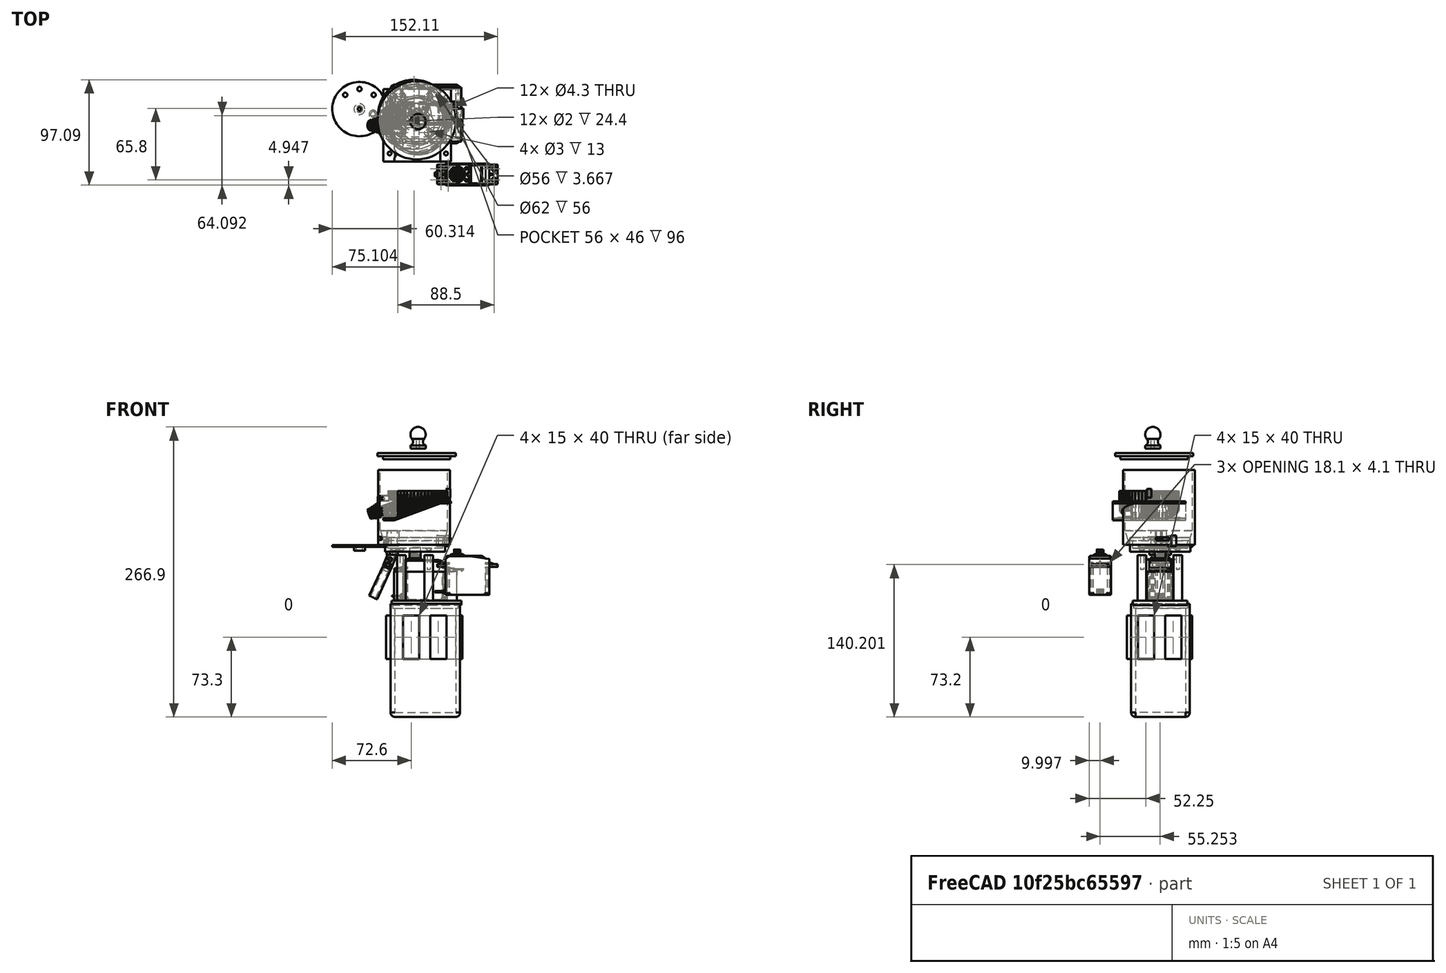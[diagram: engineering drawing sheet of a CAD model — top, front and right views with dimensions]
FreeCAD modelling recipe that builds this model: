
FCSTD DOCUMENT  (FreeCAD 0.21R33771 (Git))
Label: all_parts_chute_with_mount_v3
License: All rights reserved
LicenseURL: http://en.wikipedia.org/wiki/All_rights_reserved
objects: Part::Cylinder×37, Part::Cut×30, Part::MultiFuse×25, Part::Box×19, Part::Feature×18, Part::FeaturePython×10, Sketcher::SketchObject×3, Part::Cone×2, Part::Extrusion×2, Mesh::Feature×1, Part::Fillet×1, Part::Chamfer×1, Part::Thickness×1, PartDesign::Revolution×1, PartDesign::Body×1, Part::Wedge×1
note: 149 computed .brp shape members not serialized (recipe doc carries the construction recipe); baked Part::Feature solids carry a one-line shape summary decoded from their .brp

FEATURE [Part::Box] Box014  label="Cube014"
  AttacherType = Attacher::AttachEngine3D
  Height = 2
  Length = 7
  Placement = pos=(66.2,37.3,74.6) rot=(0,0,1;0rad)
  Width = 4.2
FEATURE [Part::Cylinder] Cylinder022
  Angle = 360
  AttacherType = Attacher::AttachEngine3D
  FirstAngle = 0
  Height = 20
  Placement = pos=(15.5,39.3,51.5) rot=(0,1,0;0.366519rad)
  Radius = 3
  SecondAngle = 0
FEATURE [Part::Box] Box015  label="Cube015"
  AttacherType = Attacher::AttachEngine3D
  Height = 10
  Length = 10
  Placement = pos=(7,34.3,72) rot=(0,0,1;0rad)
  Width = 13
FEATURE [Mesh::Feature] Base_V7  label="Base V7"
FEATURE [Part::Feature] Base_V7001_solid  label="hopper (Solid)"
  shape: bbox 76.98 x 66.8 x 28.84 mm, 5900 faces (baked)
FEATURE [Part::Feature] Shape001
  Placement = pos=(47,50.7,-44.8) rot=(0,0,1;3.14159rad)
  shape: bbox 57.75 x 20 x 41.74 mm, 378 faces, 4 solids (baked)
FEATURE [Part::Cylinder] cylinder010  label="servo_central_shaft"
  Angle = 360
  AttacherType = Attacher::AttachEngine3D
  FirstAngle = 0
  Height = 10
  Placement = pos=(37.55,50.7,-7) rot=(0,0,1;0rad)
  Radius = 5
  SecondAngle = 0
FEATURE [Part::Box] Box  label="Cube"
  AttacherType = Attacher::AttachEngine3D
  Height = 27.5
  Length = 58
  Placement = pos=(18,38.6,-47) rot=(0,0,1;0rad)
  Width = 24
FEATURE [Part::Box] Box016  label="Cube016"
  AttacherType = Attacher::AttachEngine3D
  Height = 29.5
  Length = 53
  Placement = pos=(13,46,-44) rot=(0,0,1;0rad)
  Width = 9
FEATURE [Part::Cut] Cut
  Base = -> Box
  Tool = -> Box016
FEATURE [Part::Box] Box017  label="Cube017"
  AttacherType = Attacher::AttachEngine3D
  Height = 29.5
  Length = 10
  Placement = pos=(17,46.6,-46) rot=(0,0,1;0rad)
  Width = 8
FEATURE [Part::Cut] Cut019
  Base = -> Cut
  Tool = -> Box017
FEATURE [Part::Box] Box018  label="Cube018"
  AttacherType = Attacher::AttachEngine3D
  Height = 27.5
  Length = 41
  Placement = pos=(0.5,50.4,-44.2) rot=(0,0,1;0rad)
  Width = 20.4
FEATURE [Part::Fillet] Fillet
  Base = -> Box018
  Edges = 4 edges r=1: [Edge1,Edge3,Edge5,Edge7]
  Placement = pos=(25.85,-9.87885,-1.16822) rot=(0,0,1;0rad)
FEATURE [Part::Cut] Cut020
  Base = -> Cut019
  Tool = -> Fillet
FEATURE [Part::Box] Box020  label="base_plate"
  AttacherType = Attacher::AttachEngine3D
  Height = 4
  Length = 64
  Placement = pos=(16,25.6,-50) rot=(0,0,1;0rad)
  Width = 50
FEATURE [Part::Feature] BOLTS_part  label="Hex socket countersunk head screw M3 20.0"
  Placement = pos=(25,67,2.1) rot=(0,1,0;3.14159rad)
  shape: bbox 6 x 6 x 20 mm, 12 faces (baked)
FEATURE [Part::Feature] BOLTS_part001  label="Hex socket countersunk head screw M3 20.001"
  Placement = pos=(50,67,2.1) rot=(0,1,0;3.14159rad)
  shape: bbox 6 x 6 x 20 mm, 12 faces (baked)
FEATURE [Part::Feature] BOLTS_part002  label="Hex socket countersunk head screw M3 20.002"
  Placement = pos=(50,34,2.1) rot=(0,1,0;3.14159rad)
  shape: bbox 6 x 6 x 20 mm, 12 faces (baked)
FEATURE [Part::Feature] BOLTS_part003  label="Hex socket countersunk head screw M3 20.003"
  Placement = pos=(25,34,2.1) rot=(0,1,0;3.14159rad)
  shape: bbox 6 x 6 x 20 mm, 12 faces (baked)
FEATURE [Part::Cylinder] Cylinder024
  Angle = 360
  AttacherType = Attacher::AttachEngine3D
  FirstAngle = 0
  Height = 45
  Placement = pos=(50,67,-49) rot=(0,0,1;0rad)
  Radius = 4
  SecondAngle = 0
FEATURE [Part::Cylinder] Cylinder025
  Angle = 360
  AttacherType = Attacher::AttachEngine3D
  FirstAngle = 0
  Height = 45
  Placement = pos=(25,34,-49) rot=(0,0,1;0rad)
  Radius = 4
  SecondAngle = 0
FEATURE [Part::Cylinder] Cylinder026
  Angle = 360
  AttacherType = Attacher::AttachEngine3D
  FirstAngle = 0
  Height = 45
  Placement = pos=(25,67,-49) rot=(0,0,1;0rad)
  Radius = 4
  SecondAngle = 0
FEATURE [Part::Cylinder] Cylinder027
  Angle = 360
  AttacherType = Attacher::AttachEngine3D
  FirstAngle = 0
  Height = 45
  Placement = pos=(50,34,-49) rot=(0,0,1;0rad)
  Radius = 4
  SecondAngle = 0
FEATURE [Part::Feature] Shape002  label="led2"
  Placement = pos=(14.5,42.3,-8) rot=(-1,0,0;1.5708rad)
  shape: bbox 3.686 x 11.4 x 3.686 mm, 26 faces, 3 solids (baked)
FEATURE [Part::Feature] Shape003  label="led1"
  Placement = pos=(14.5,59.1,-8) rot=(1,0,0;1.5708rad)
  shape: bbox 3.686 x 11.4 x 3.686 mm, 26 faces, 3 solids (baked)
FEATURE [Part::Feature] BOLTS_part004  label="Hex socket countersunk head screw M3 20.004"
  Placement = pos=(25,34,3) rot=(0,1,0;3.14159rad)
  shape: bbox 6 x 6 x 20 mm, 12 faces (baked)
FEATURE [Part::Feature] BOLTS_part005  label="Hex socket countersunk head screw M3 20.005"
  Placement = pos=(50,34,3) rot=(0,1,0;3.14159rad)
  shape: bbox 6 x 6 x 20 mm, 12 faces (baked)
FEATURE [Part::Feature] BOLTS_part006  label="Hex socket countersunk head screw M3 20.006"
  Placement = pos=(50,67,3) rot=(0,1,0;3.14159rad)
  shape: bbox 6 x 6 x 20 mm, 12 faces (baked)
FEATURE [Part::Feature] BOLTS_part007  label="Hex socket countersunk head screw M3 20.007"
  Placement = pos=(25,67,3) rot=(0,1,0;3.14159rad)
  shape: bbox 6 x 6 x 20 mm, 12 faces (baked)
FEATURE [Part::Cylinder] Cylinder032
  Angle = 360
  AttacherType = Attacher::AttachEngine3D
  FirstAngle = 0
  Height = 48
  Placement = pos=(50,67,-43) rot=(0,0,1;0rad)
  Radius = 1.4
  SecondAngle = 0
FEATURE [Part::Cylinder] Cylinder033
  Angle = 360
  AttacherType = Attacher::AttachEngine3D
  FirstAngle = 0
  Height = 48
  Placement = pos=(25,34,-43) rot=(0,0,1;0rad)
  Radius = 1.4
  SecondAngle = 0
FEATURE [Part::Cylinder] Cylinder034
  Angle = 360
  AttacherType = Attacher::AttachEngine3D
  FirstAngle = 0
  Height = 48
  Placement = pos=(25,67,-42) rot=(0,0,1;0rad)
  Radius = 1.4
  SecondAngle = 0
FEATURE [Part::Cylinder] Cylinder035
  Angle = 360
  AttacherType = Attacher::AttachEngine3D
  FirstAngle = 0
  Height = 48
  Placement = pos=(50,34,-43) rot=(0,0,1;0rad)
  Radius = 1.4
  SecondAngle = 0
FEATURE [Part::Cut] Cut030
  Base = -> Cylinder024
  Tool = -> BOLTS_part006
FEATURE [Part::Cut] Cut031
  Base = -> Cylinder025
  Tool = -> BOLTS_part004
FEATURE [Part::Cut] Cut032
  Base = -> Cylinder026
  Tool = -> BOLTS_part007
FEATURE [Part::Cut] Cut033
  Base = -> Cylinder027
  Tool = -> BOLTS_part005
FEATURE [Part::MultiFuse] Fusion011  label="fusion"
  Shapes = -> [Cut020,Cut030,Cut031,Cut032,Cut033,Box020]
FEATURE [Part::Cylinder] Cylinder039
  Angle = 360
  AttacherType = Attacher::AttachEngine3D
  FirstAngle = 0
  Height = 21
  Placement = pos=(0,10,6) rot=(1,0,0;1.5708rad)
  Radius = 1.6
  SecondAngle = 0
FEATURE [Part::FeaturePython] Tube003  # WARN: FeaturePython — macro-defined, semantics opaque (R4)
  AttacherType = Attacher::AttachEngine3D
  Height = 5
  InnerRadius = 1.5
  OuterRadius = 2.5
  Placement = pos=(0,2.05,6) rot=(-1,0,0;1.5708rad)
FEATURE [Part::FeaturePython] Tube004  # WARN: FeaturePython — macro-defined, semantics opaque (R4)
  AttacherType = Attacher::AttachEngine3D
  Height = 5
  InnerRadius = 1.5
  OuterRadius = 2.5
  Placement = pos=(0,-2.05,6) rot=(1,0,0;1.5708rad)
FEATURE [Part::Box] Box021  label="Cube019"
  AttacherType = Attacher::AttachEngine3D
  Height = 10
  Length = 20
  Placement = pos=(1.17,-11.94,17.9) rot=(0,0,1;0rad)
  Width = 24
FEATURE [Part::FeaturePython] Tube001  # WARN: FeaturePython — macro-defined, semantics opaque (R4)
  AttacherType = Attacher::AttachEngine3D
  Height = 3
  InnerRadius = 15
  OuterRadius = 27.7
  Placement = pos=(40.45,39.4,63.6) rot=(0,0,1;0rad)
FEATURE [Part::FeaturePython] Tube002  # WARN: FeaturePython — macro-defined, semantics opaque (R4)
  AttacherType = Attacher::AttachEngine3D
  Height = 13
  InnerRadius = 25.3
  OuterRadius = 27.7
  Placement = pos=(40.45,39.4,63.6) rot=(0,0,1;0rad)
FEATURE [Part::MultiFuse] Fusion009
  Shapes = -> [Box014,Tube001,Tube002]
FEATURE [Part::Cut] Cut014  label="cut"
  Base = -> Fusion009
  Tool = -> Cylinder022
FEATURE [Part::Cut] Cut036
  Base = -> Cut014
  Placement = pos=(-2.9,11.3,-64.5) rot=(0,0,1;0rad)
  Tool = -> Box015
FEATURE [Part::MultiFuse] Fusion
  Shapes = -> [BOLTS_part003,Cylinder033]
FEATURE [Part::MultiFuse] Fusion013
  Shapes = -> [BOLTS_part002,Cylinder035]
FEATURE [Part::MultiFuse] Fusion014
  Shapes = -> [BOLTS_part001,Cylinder032]
FEATURE [Part::MultiFuse] Fusion015
  Shapes = -> [BOLTS_part,Cylinder034]
FEATURE [Part::Cut] Cut037
  Base = -> Cut036
  Tool = -> Fusion
FEATURE [Part::Cut] Cut038
  Base = -> Cut037
  Tool = -> Fusion013
FEATURE [Part::Cut] Cut039
  Base = -> Cut038
  Tool = -> Fusion015
FEATURE [Part::Cut] Cut040
  Base = -> Cut039
  Tool = -> Fusion014
FEATURE [Part::Feature] BOLTS_part009  label="Hex socket countersunk head screw M3 20.008"
  Placement = pos=(50,34,2.1) rot=(0,1,0;3.14159rad)
  shape: bbox 6 x 6 x 20 mm, 12 faces (baked)
FEATURE [Part::Cylinder] Cylinder040
  Angle = 360
  AttacherType = Attacher::AttachEngine3D
  FirstAngle = 0
  Height = 48
  Placement = pos=(50,34,-43) rot=(0,0,1;0rad)
  Radius = 1.4
  SecondAngle = 0
FEATURE [Part::MultiFuse] Fusion016
  Placement = pos=(-32,9,0) rot=(0,0,1;0rad)
  Shapes = -> [BOLTS_part009,Cylinder040]
FEATURE [Part::Feature] BOLTS_part010  label="Hex socket countersunk head screw M3 20.009"
  Placement = pos=(50,34,2.1) rot=(0,1,0;3.14159rad)
  shape: bbox 6 x 6 x 20 mm, 12 faces (baked)
FEATURE [Part::Cylinder] Cylinder041
  Angle = 360
  AttacherType = Attacher::AttachEngine3D
  FirstAngle = 0
  Height = 48
  Placement = pos=(50,34,-43) rot=(0,0,1;0rad)
  Radius = 1.4
  SecondAngle = 0
FEATURE [Part::MultiFuse] Fusion017
  Placement = pos=(-32,24,0) rot=(0,0,1;0rad)
  Shapes = -> [BOLTS_part010,Cylinder041]
FEATURE [Part::Box] Box022  label="Cube020"
  AttacherType = Attacher::AttachEngine3D
  Height = 3
  Length = 10
  Placement = pos=(3,-10,15) rot=(0,0,1;0rad)
  Width = 20
FEATURE [Part::Cylinder] Cylinder
  Angle = 360
  AttacherType = Attacher::AttachEngine3D
  FirstAngle = 0
  Height = 18
  Radius = 4
  SecondAngle = 0
FEATURE [Part::Cut] Cut043
  Base = -> Cylinder
  Tool = -> Cylinder039
FEATURE [Part::MultiFuse] Fusion018
  Placement = pos=(2,0,0) rot=(0,1,0;0.366519rad)
  Shapes = -> [Tube003,Tube004,Cut043]
FEATURE [Part::MultiFuse] Fusion019
  Shapes = -> [Fusion018,Box022]
FEATURE [Part::Feature] BOLTS_part011  label="Hex socket countersunk head screw M3 20.010"
  Placement = pos=(50,34,2.1) rot=(0,1,0;3.14159rad)
  shape: bbox 6 x 6 x 20 mm, 12 faces (baked)
FEATURE [Part::Cylinder] Cylinder044
  Angle = 360
  AttacherType = Attacher::AttachEngine3D
  FirstAngle = 0
  Height = 48
  Placement = pos=(50,34,-43) rot=(0,0,1;0rad)
  Radius = 1.4
  SecondAngle = 0
FEATURE [Part::MultiFuse] Fusion021
  Placement = pos=(-32,9,0) rot=(0,0,1;0rad)
  Shapes = -> [BOLTS_part011,Cylinder044]
FEATURE [Part::Feature] BOLTS_part012  label="Hex socket countersunk head screw M3 20.011"
  Placement = pos=(50,34,2.1) rot=(0,1,0;3.14159rad)
  shape: bbox 6 x 6 x 20 mm, 12 faces (baked)
FEATURE [Part::Cylinder] Cylinder045
  Angle = 360
  AttacherType = Attacher::AttachEngine3D
  FirstAngle = 0
  Height = 48
  Placement = pos=(50,34,-43) rot=(0,0,1;0rad)
  Radius = 1.4
  SecondAngle = 0
FEATURE [Part::MultiFuse] Fusion022
  Placement = pos=(-32,24,0) rot=(0,0,1;0rad)
  Shapes = -> [BOLTS_part012,Cylinder045]
FEATURE [Part::Cut] Cut047
  Base = -> Cut040
  Tool = -> Fusion016
FEATURE [Part::Cut] Cut048
  Base = -> Cut047
  Tool = -> Fusion017
FEATURE [Part::Feature] Shape004  label="Servo_motor"
  Placement = pos=(46.0641,51.1469,-44.6487) rot=(0,0,1;3.14159rad)
  shape: bbox 57.75 x 20 x 41.74 mm, 378 faces, 4 solids (baked)
FEATURE [Part::Box] Box012  label="Cube012"
  AttacherType = Attacher::AttachEngine3D
  Height = 10
  Length = 10
  Placement = pos=(7,36.17,76) rot=(0,0,1;0rad)
  Width = 6
FEATURE [Part::Box] Box013  label="Cube013"
  AttacherType = Attacher::AttachEngine3D
  Height = 3
  Length = 14
  Placement = pos=(64,38,58) rot=(0,0,1;0rad)
  Width = 12
FEATURE [Part::Cone] Cone
  Angle = 360
  AttacherType = Attacher::AttachEngine3D
  Height = 14
  Placement = pos=(40,40.65,53) rot=(0,0,1;0rad)
  Radius1 = 26.5
  Radius2 = 31
FEATURE [Part::Cylinder] Cylinder019
  Angle = 360
  AttacherType = Attacher::AttachEngine3D
  FirstAngle = 0
  Height = 13
  Placement = pos=(40,40.65,54) rot=(0,0,1;0rad)
  Radius = 33
  SecondAngle = 0
FEATURE [Part::Cylinder] Cylinder020
  Angle = 360
  AttacherType = Attacher::AttachEngine3D
  FirstAngle = 0
  Height = 13
  Placement = pos=(40,39.2,54) rot=(0,0,1;0rad)
  Radius = 25
  SecondAngle = 0
FEATURE [Part::Cylinder] Cylinder021
  Angle = 360
  AttacherType = Attacher::AttachEngine3D
  FirstAngle = 0
  Height = 4
  Placement = pos=(40,40.65,54) rot=(0,0,1;0rad)
  Radius = 28
  SecondAngle = 0
FEATURE [Sketcher::SketchObject] Sketch001
  FullyConstrained = true
  MapMode = 2
  Placement = pos=(0,5,65) rot=(0,0,1;0rad)
  sketch-geometry (8):
    g0: ArcOfCircle CenterX=20.555 CenterY=41.4363 CenterZ=0 NormalX=0 NormalY=0 NormalZ=1 AngleXU=0 Radius=4.5 StartAngle=3.17145 EndAngle=4.38602
    g1: ArcOfCircle CenterX=24.0176 CenterY=34.022 CenterZ=0 NormalX=0 NormalY=0 NormalZ=1 AngleXU=0 Radius=2 StartAngle=5.10518 EndAngle=7.46119
    g2: ArcOfCircle CenterX=20.5312 CenterY=26.882 CenterZ=0 NormalX=0 NormalY=0 NormalZ=1 AngleXU=0 Radius=4.5 StartAngle=1.8916 EndAngle=3.11914
    g3: LineSegment StartX=19.1123 StartY=31.1525 StartZ=0 EndX=24.7831 EndY=32.1743 EndZ=0
    g4: LineSegment StartX=19.1123 StartY=37.1738 StartZ=0 EndX=24.7831 EndY=35.8697 EndZ=0
    g5: LineSegment StartX=16.057 StartY=41.302 StartZ=0 EndX=15.8089 EndY=41.3763 EndZ=0
    g6: LineSegment StartX=15.8133 StartY=26.9187 StartZ=0 EndX=16.0324 EndY=26.9831 EndZ=0
    g7: ArcOfCircle CenterX=39.7432 CenterY=34.1548 CenterZ=0 NormalX=0 NormalY=0 NormalZ=1 AngleXU=0 Radius=25 StartAngle=2.84856 EndAngle=3.43524
  constraints (28):
    c: Coincident(g3,g2)
    c: Coincident(g3,g1)
    c: Coincident(g4,g0)
    c: Coincident(g4,g1)
    c: Coincident(g5,g0)
    c: Coincident(g6,g2)
    c: Coincident(g7,g6)
    c: Coincident(g7,g5)
    c: Radius(g2) = 4.5
    c: Radius(g0) = 4.5
    c: Radius(g1) = 2
    c: Radius(g7) = 25
    c: DistanceX(g5) = 15.8089
    c: DistanceY(g5) = 41.3763
    c: DistanceX(g2) = 16.0324
    c: DistanceY(g2) = 26.9831
    c: DistanceX(g3) = 19.1123
    c: DistanceY(g3) = 31.1525
    c: DistanceX(g2,g0) = 0
    c: DistanceX(g3,g1) = 0
    c: DistanceX(g1) = 24.7831
    c: DistanceY(g1) = 32.1743
    c: DistanceX(g5) = 16.057
    c: DistanceY(g5) = 41.302
    c: DistanceX(g7) = 15.8133
    c: DistanceY(g7) = 26.9187
    c: DistanceY(g1) = 35.8697
    c: DistanceY(g0) = 37.1738
FEATURE [Part::Extrusion] Extrude001
  Base = -> Sketch001
  Dir = (0,0,1)
  DirMode = 2
  FaceMakerClass = Part::FaceMakerBullseye
  LengthFwd = 14
  LengthRev = 0
  Placement = pos=(0,0,7) rot=(0,0,1;0rad)
  Solid = true
  Symmetric = false
FEATURE [Part::MultiFuse] Fusion006  label="pellet_sorter"
  Placement = pos=(0,1.5,-19) rot=(0,0,1;0rad)
  Shapes = -> [Box012,Extrude001]
FEATURE [Part::FeaturePython] Tube  # WARN: FeaturePython — macro-defined, semantics opaque (R4)
  AttacherType = Attacher::AttachEngine3D
  Height = 69
  InnerRadius = 31
  OuterRadius = 33
  Placement = pos=(40,40.65,54) rot=(0,0,1;0rad)
FEATURE [Part::MultiFuse] Fusion010
  Shapes = -> [Tube,Cylinder019,Cylinder020]
FEATURE [Part::Cut] Cut015
  Base = -> Fusion010
  Tool = -> Cone
FEATURE [Part::Cut] Cut016
  Base = -> Cut015
  Tool = -> Cylinder021
FEATURE [Part::MultiFuse] Fusion024
  Shapes = -> [Fusion006,Cut016]
FEATURE [Part::Cut] Cut017  label="cut002"
  Base = -> Fusion024
  Placement = pos=(2.75889,1.57596,-47) rot=(0,0,1;0.15708rad)
  Tool = -> Box013
FEATURE [Part::Cylinder] Cylinder047
  Angle = 360
  AttacherType = Attacher::AttachEngine3D
  FirstAngle = 0
  Height = 3
  Radius = 36
  SecondAngle = 0
FEATURE [Part::Cylinder] Cylinder048
  Angle = 360
  AttacherType = Attacher::AttachEngine3D
  FirstAngle = 0
  Height = 6
  Radius = 31
  SecondAngle = 0
FEATURE [Part::MultiFuse] Fusion025  label="cut001"
  Placement = pos=(39,45.2,90) rot=(1,0,0;3.14159rad)
  Shapes = -> [Cylinder047,Cylinder048]
FEATURE [Part::Cylinder] cylinder012
  Angle = 360
  AttacherType = Attacher::AttachEngine3D
  FirstAngle = 0
  Height = 1.5
  Radius = 25
  SecondAngle = 0
FEATURE [Part::Cylinder] cylinder013
  Angle = 360
  AttacherType = Attacher::AttachEngine3D
  FirstAngle = 0
  Height = 1
  Placement = pos=(18.5,0,0) rot=(0,0,1;0rad)
  Radius = 2
  SecondAngle = 0
FEATURE [Part::Cylinder] cylinder014
  Angle = 360
  AttacherType = Attacher::AttachEngine3D
  FirstAngle = 0
  Height = 1
  Placement = pos=(13.0815,13.0815,0) rot=(0,0,1;0.785398rad)
  Radius = 2
  SecondAngle = 0
FEATURE [Part::Cylinder] cylinder015
  Angle = 360
  AttacherType = Attacher::AttachEngine3D
  FirstAngle = 0
  Height = 1
  Placement = pos=(0,18.5,0) rot=(0,0,1;1.5708rad)
  Radius = 2
  SecondAngle = 0
FEATURE [Part::Cylinder] cylinder016
  Angle = 360
  AttacherType = Attacher::AttachEngine3D
  FirstAngle = 0
  Height = 1
  Placement = pos=(-13.0815,13.0815,0) rot=(0,0,1;2.35619rad)
  Radius = 2
  SecondAngle = 0
FEATURE [Part::Cylinder] cylinder017
  Angle = 360
  AttacherType = Attacher::AttachEngine3D
  FirstAngle = 0
  Height = 1
  Placement = pos=(-18.5,2e-15,0) rot=(0,0,1;3.14159rad)
  Radius = 2
  SecondAngle = 0
FEATURE [Part::Cylinder] cylinder018
  Angle = 360
  AttacherType = Attacher::AttachEngine3D
  FirstAngle = 0
  Height = 5
  Placement = pos=(-13.0815,-13.0815,0) rot=(0,0,1;3.92699rad)
  Radius = 2
  SecondAngle = 0
FEATURE [Part::Cylinder] cylinder019
  Angle = 360
  AttacherType = Attacher::AttachEngine3D
  FirstAngle = 0
  Height = 5
  Placement = pos=(0,-18.5,0) rot=(0,0,-1;1.5708rad)
  Radius = 2
  SecondAngle = 0
FEATURE [Part::Cylinder] cylinder020
  Angle = 360
  AttacherType = Attacher::AttachEngine3D
  FirstAngle = 0
  Height = 5
  Placement = pos=(13.0815,-13.0815,0) rot=(0,0,-1;0.785398rad)
  Radius = 2
  SecondAngle = 0
FEATURE [Part::MultiFuse] Group001
  Placement = pos=(0,0,-1) rot=(0,0,1;0rad)
  Shapes = -> [cylinder013,cylinder014,cylinder015,cylinder016,cylinder017,cylinder018,cylinder019,cylinder020]
FEATURE [Part::Feature] Shape005
  Placement = pos=(85.6641,-4.55315,-40.6487) rot=(0,0,1;3.14159rad)
  shape: bbox 57.75 x 20 x 41.74 mm, 378 faces, 4 solids (baked)
FEATURE [Part::Cylinder] cylinder021  label="servo_central_shaft002"
  Angle = 360
  AttacherType = Attacher::AttachEngine3D
  FirstAngle = 0
  Height = 5
  Radius = 5
  SecondAngle = 0
FEATURE [Sketcher::SketchObject] Sketch002
  FullyConstrained = false
  MapMode = 5
  Placement = pos=(85.6641,-4.55315,1.09128) rot=(0,0,1;3.14159rad)
  Support = -> [Shape005]
  sketch-geometry (1):
    g0: Circle CenterX=9.4502 CenterY=-0.000218 CenterZ=0 NormalX=0 NormalY=0 NormalZ=1 AngleXU=0 Radius=3
  constraints (1):
    c: Radius(g0) = 3
FEATURE [Part::Extrusion] Extrude002
  Base = -> Sketch002
  Dir = (0,0,1)
  DirMode = 2
  FaceMakerClass = Part::FaceMakerBullseye
  LengthFwd = 4
  LengthRev = 3.4
  Placement = pos=(-76.21,4.55,3) rot=(0,0,1;0rad)
  Solid = true
  Symmetric = false
FEATURE [Part::Cylinder] Cylinder049
  Angle = 360
  AttacherType = Attacher::AttachEngine3D
  FirstAngle = 0
  Height = 19
  Placement = pos=(0,0,-1) rot=(0,0,1;0rad)
  Radius = 1.5
  SecondAngle = 0
FEATURE [Part::MultiFuse] Fusion026
  Shapes = -> [Group001,Extrude002,Cylinder049]
FEATURE [Part::MultiFuse] Fusion027
  Shapes = -> [cylinder012,cylinder021]
FEATURE [Part::Cut] Cut050  label="Rotor"
  Base = -> Fusion027
  Placement = pos=(-13.7,55.5,5) rot=(1,0,0;3.14159rad)
  Tool = -> Fusion026
FEATURE [Part::Cone] Cone001
  Angle = 360
  AttacherType = Attacher::AttachEngine3D
  Height = 11
  Placement = pos=(0,-29,0) rot=(0,0,1;0rad)
  Radius1 = 2
  Radius2 = 3
FEATURE [Part::Cylinder] Cylinder050
  Angle = 360
  AttacherType = Attacher::AttachEngine3D
  FirstAngle = 0
  Height = 10
  Placement = pos=(0,-29,-10) rot=(0,0,1;0rad)
  Radius = 2
  SecondAngle = 0
FEATURE [Part::Cylinder] Cylinder051
  Angle = 360
  AttacherType = Attacher::AttachEngine3D
  FirstAngle = 0
  Height = 14
  Placement = pos=(0,-29,11) rot=(0,0,1;0rad)
  Radius = 2
  SecondAngle = 0
FEATURE [Part::MultiFuse] Fusion028
  Placement = pos=(5,29,8) rot=(0,1,0;0.366519rad)
  Shapes = -> [Cone001,Cylinder050,Cylinder051]
FEATURE [Part::MultiFuse] Fusion020
  Shapes = -> [Box021,Fusion028]
FEATURE [Part::Cut] Cut044  label="foodchute"
  Base = -> Fusion019
  Placement = pos=(8.45427,50.6,-18.8) rot=(0,0,1;0rad)
  Tool = -> Fusion020
FEATURE [Part::Chamfer] Chamfer
  Base = -> Cut044
  Edges = 2 edges r=3: [Edge1,Edge3]
FEATURE [Part::Cut] Cut045
  Base = -> Chamfer
  Tool = -> Fusion021
FEATURE [Part::Cut] Cut046
  Base = -> Cut045
  Tool = -> Fusion022
FEATURE [Part::FeaturePython] Tube005  # WARN: FeaturePython — macro-defined, semantics opaque (R4)
  AttacherType = Attacher::AttachEngine3D
  Height = 4
  InnerRadius = 3
  OuterRadius = 5
  Placement = pos=(10.2596,50.6,-19.2425) rot=(0,1,0;0.401426rad)
FEATURE [Part::Cut] Cut051  label="chute_with_mount"
  Base = -> Cut046
  Tool = -> Tube005
FEATURE [Part::Box] Box023  label="Cube021"
  AttacherType = Attacher::AttachEngine3D
  Height = 100
  Length = 56
  Width = 46
FEATURE [Part::Thickness] Thickness
  Faces = -> Box023 [Face5]
  Intersection = false
  Join = 0
  Mode = 0
  SelfIntersection = false
  Value = 4
FEATURE [Part::Box] Box001  label="Cube001"
  AttacherType = Attacher::AttachEngine3D
  Height = 4
  Length = 60
  Placement = pos=(-2,-2,0) rot=(0,0,1;0rad)
  Width = 50
FEATURE [Part::Box] Box024  label="Cube022"
  AttacherType = Attacher::AttachEngine3D
  Height = 40
  Length = 15
  Placement = pos=(26.4,20,-99.7) rot=(0,0,1;0rad)
  Width = 60
FEATURE [Part::Box] Box025  label="Cube023"
  AttacherType = Attacher::AttachEngine3D
  Height = 40
  Length = 70
  Placement = pos=(10.9,30.2,-99.8) rot=(0,0,1;0rad)
  Width = 15
FEATURE [Part::Cylinder] Cylinder052
  Angle = 360
  AttacherType = Attacher::AttachEngine3D
  FirstAngle = 0
  Height = 10
  Placement = pos=(39,45.2,83) rot=(0,0,1;0rad)
  Radius = 1.5
  SecondAngle = 0
FEATURE [Part::Cut] Cut055  label="Cap"
  Base = -> Fusion025
  Tool = -> Cylinder052
FEATURE [Sketcher::SketchObject] Sketch
  FullyConstrained = true
  MapMode = 5
  Placement = pos=(0,0,0) rot=(0.57735,0.57735,0.57735;2.0944rad)
  Support = -> [YZ_Plane]
  sketch-geometry (7):
    g0: LineSegment StartX=-7 StartY=0 StartZ=0 EndX=-7 EndY=3 EndZ=0
    g1: ArcOfCircle CenterX=-8.02642 CenterY=6.34611 CenterZ=0 NormalX=0 NormalY=0 NormalZ=1 AngleXU=0 Radius=3.5 StartAngle=5.01003 EndAngle=7.14382
    g2: ArcOfCircle CenterX=0 CenterY=13 CenterZ=0 NormalX=0 NormalY=0 NormalZ=1 AngleXU=0 Radius=7 StartAngle=1.5708 EndAngle=3.74984
    g3: LineSegment StartX=-7 StartY=0 StartZ=0 EndX=-1.55 EndY=0 EndZ=0
    g4: LineSegment StartX=-1.55 StartY=0 StartZ=0 EndX=-1.55 EndY=9 EndZ=0
    g5: LineSegment StartX=-1.55 StartY=9 StartZ=0 EndX=0 EndY=9 EndZ=0
    g6: LineSegment StartX=0 StartY=9 StartZ=0 EndX=4e-16 EndY=20 EndZ=0
  constraints (23):
    c: PointOnObject(g0,g-1)
    c: Coincident(g1,g0)
    c: PointOnObject(g2,g-2)
    c: Coincident(g2,g1)
    c: PointOnObject(g2,g-2)
    c: DistanceX(g0,g-1) = 7
    c: Vertical(g0)
    c: DistanceY(g0,g0) = 3
    c: Diameter(g1) = 7
    c: Diameter(g2) = 14
    c: DistanceY(g-1,g2) = 20
    c: DistanceY(g-1,g1) = 9
    c: Coincident(g3,g0)
    c: PointOnObject(g3,g-1)
    c: Coincident(g4,g3)
    c: Vertical(g4)
    c: PointOnObject(g5,g-2)
    c: Horizontal(g5)
    c: Coincident(g6,g5)
    c: Coincident(g6,g2)
    c: DistanceX(g3,g-1) = 1.55
    c: DistanceY(g4,g4) = 9
    c: Coincident(g5,g4)
FEATURE [PartDesign::Revolution] Revolution
  Angle = 360
  Axis = (-2e-16,3e-16,1)
  Base = (0,0,0)
  Placement = pos=(0,0,0) rot=(0.57735,0.57735,0.57735;2.0944rad)
  Profile = -> Sketch
  ReferenceAxis = -> Sketch [V_Axis]
FEATURE [PartDesign::Body] Body  label="Handle"
  Group = -> [Sketch,Revolution]
  Origin = -> Origin
  Placement = pos=(40.2,44,93.9) rot=(0,0,1;0rad)
  Tip = -> Revolution
FEATURE [Part::Cylinder] Cylinder053
  Angle = 360
  AttacherType = Attacher::AttachEngine3D
  FirstAngle = 0
  Height = 30
  Radius = 4
  SecondAngle = 0
FEATURE [Part::Cylinder] Cylinder054
  Angle = 360
  AttacherType = Attacher::AttachEngine3D
  FirstAngle = 0
  Height = 30
  Radius = 2.5
  SecondAngle = 0
FEATURE [Part::Cut] Cut056  label="Flextube"
  Base = -> Cylinder053
  Placement = pos=(-1.21802,50.6,-43.0177) rot=(0,1,0;0.436332rad)
  Tool = -> Cylinder054
FEATURE [Part::FeaturePython] Array  # Draft array (typed FeaturePython)
  AlwaysSyncPlacement = false
  Angle = 360
  ArrayType = 0
  Axis = (0,0,1)
  Base = -> Box024
  Center = (0,0,0)
  Count = 2
  ExpandArray = false
  Fuse = false
  IntervalAxis = (0,0,0)
  IntervalX = (25,0,0)
  IntervalY = (0,100,0)
  IntervalZ = (0,0,100)
  NumberCircles = 3
  NumberPolar = 5
  NumberX = 2
  NumberY = 1
  NumberZ = 1
  PlacementList = 2 placements: [(26.4,20,-99.7),(51.4,20,-99.7)]
  RadialDistance = 50
  ScaleList = (2) [(1,1,1),(1,1,1)]
  Symmetry = 1
  TangentialDistance = 25
FEATURE [Part::Cut] Cut052  label="cube"
  Base = -> Thickness
  Placement = pos=(18.9,74,-49) rot=(1,0,0;3.14159rad)
  Tool = -> Box001
FEATURE [Part::Cut] Cut057
  Base = -> Cut052
  Tool = -> Array
FEATURE [Part::FeaturePython] Array001  # Draft array (typed FeaturePython)
  AlwaysSyncPlacement = false
  Angle = 360
  ArrayType = 0
  Axis = (0,0,1)
  Base = -> Box025
  Center = (0,0,0)
  Count = 2
  ExpandArray = false
  Fuse = false
  IntervalAxis = (0,0,0)
  IntervalX = (100,0,0)
  IntervalY = (0,25,0)
  IntervalZ = (0,0,100)
  NumberCircles = 3
  NumberPolar = 5
  NumberX = 1
  NumberY = 2
  NumberZ = 1
  PlacementList = 2 placements: [(10.9,30.2,-99.8),(10.9,55.2,-99.8)]
  RadialDistance = 50
  ScaleList = (2) [(1,1,1),(1,1,1)]
  Symmetry = 1
  TangentialDistance = 25
FEATURE [Part::Cut] Cut058  label="Platform"
  Base = -> Cut057
  Tool = -> Array001
FEATURE [Part::Box] Box026  label="Cube024"
  AttacherType = Attacher::AttachEngine3D
  Height = 10
  Length = 10
  Placement = pos=(59,57.4,4) rot=(0,0,1;0.349066rad)
  Width = 5
FEATURE [Part::Box] Box027  label="Cube025"
  AttacherType = Attacher::AttachEngine3D
  Height = 2
  Length = 7
  Placement = pos=(5.9,41.5,10.3) rot=(0,0,1;0rad)
  Width = 4.2
FEATURE [Part::MultiFuse] Fusion029  label="base"
  Shapes = -> [Box027,Cut048]
FEATURE [Part::FeaturePython] Array002  # Draft array (typed FeaturePython)
  AlwaysSyncPlacement = false
  Angle = 360
  ArrayType = 1
  Axis = (0,0,1)
  Base = -> Box026
  Center = (36,47,0)
  Count = 2
  ExpandArray = false
  Fuse = false
  IntervalAxis = (0,0,0)
  IntervalX = (50,0,0)
  IntervalY = (0,50,0)
  IntervalZ = (0,0,50)
  NumberCircles = 3
  NumberPolar = 2
  NumberX = 2
  NumberY = 2
  NumberZ = 1
  Placement = pos=(0,-1.6,0.4) rot=(0,0,1;0rad)
  PlacementList = 2 placements: [(59,57.4,4),(13,36.6,4)]
  RadialDistance = 50
  ScaleList = (2) [(1,1,1),(1,1,1)]
  Symmetry = 1
  TangentialDistance = 25
FEATURE [Part::FeaturePython] Array003  # Draft array (typed FeaturePython)
  AlwaysSyncPlacement = false
  Angle = 360
  ArrayType = 1
  Axis = (0,0,1)
  Base = -> Box013
  Center = (33,47,0)
  Count = 2
  ExpandArray = false
  Fuse = false
  IntervalAxis = (0,0,0)
  IntervalX = (50,0,0)
  IntervalY = (0,50,0)
  IntervalZ = (0,0,50)
  NumberCircles = 3
  NumberPolar = 2
  NumberX = 2
  NumberY = 2
  NumberZ = 1
  Placement = pos=(22.8297,-12.422,-46.6) rot=(0,0,1;0.244346rad)
  PlacementList = 2 placements: [(64,38,58),(2,56,58)]
  RadialDistance = 50
  ScaleList = (2) [(1,1,1),(1,1,1)]
  Symmetry = 1
  TangentialDistance = 25
FEATURE [Part::MultiFuse] Fusion030
  Shapes = -> [Array003,Array002]
FEATURE [Part::Cut] Cut059  label="Feed_tank"
  Base = -> Cut017
  Placement = pos=(-6.56718,7.76741,-1.6) rot=(0,0,-1;0.15708rad)
  Tool = -> Fusion030
FEATURE [Part::Box] Box028  label="Cube026"
  AttacherType = Attacher::AttachEngine3D
  Height = 6
  Length = 1
  Width = 10
FEATURE [Part::Box] Box029  label="Cube027"
  AttacherType = Attacher::AttachEngine3D
  Height = 1
  Length = 5
  Width = 10
FEATURE [Part::Wedge] Wedge
  AttacherType = Attacher::AttachEngine3D
  Placement = pos=(5,10,-1) rot=(0,0,1;4.71239rad)
  X2max = 10
  X2min = 1
  Xmax = 10
  Xmin = 0
  Ymax = 2
  Ymin = 0
  Z2max = 2
  Z2min = 1
  Zmax = 3.5
  Zmin = 1
FEATURE [Part::MultiFuse] Fusion031
  Placement = pos=(75,56,-16.5) rot=(1,0,0;3.14159rad)
  Shapes = -> [Wedge,Box029,Box028]
FEATURE [Part::MultiFuse] Fusion032  label="Motor_holder"
  Shapes = -> [Fusion031,Fusion011]
